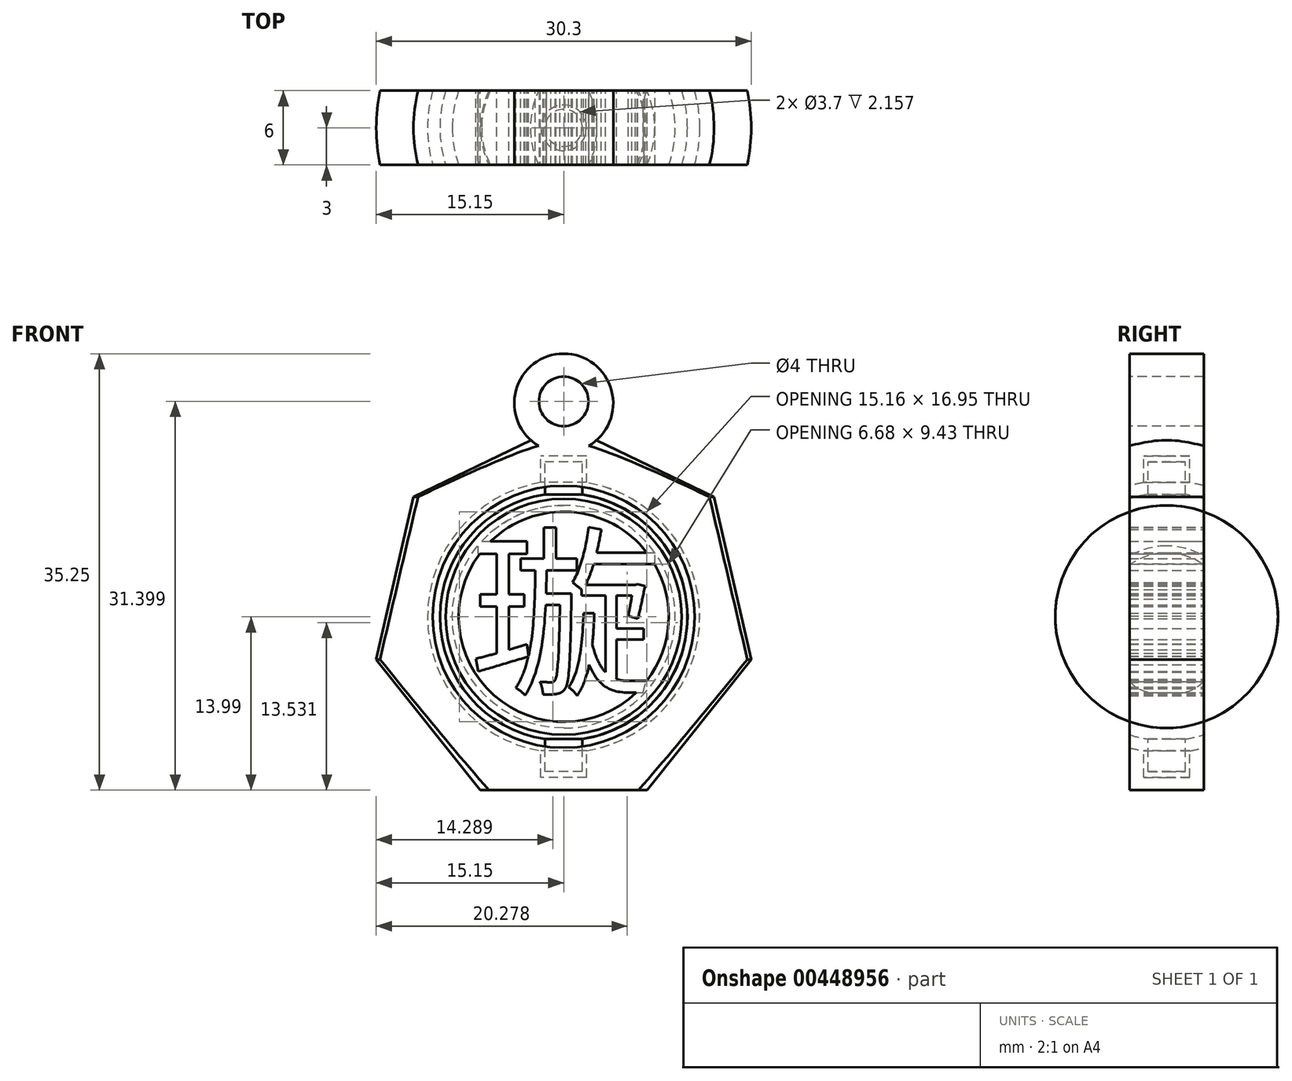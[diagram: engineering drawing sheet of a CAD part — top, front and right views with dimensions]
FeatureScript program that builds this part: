
annotation { "Feature Type Name" : "Feature", "Feature Type Description" : "" }
export const myFeature = defineFeature(function(context is Context, id is Id, definition is map)
    precondition{}
    {
        {
            var Q0;
            Q0=qCreatedBy(makeId("Front.planeOp"),FACE);
            var sketch = newSketch(context, id + "F0", { "sketchPlane" : qUnion([Q0])});
            skLineSegment(sketch, "E0.bottom", {"start": v(1.85, -13) * mm, "end": v(-1.85, -13) * mm});
            skLineSegment(sketch, "E0.top", {"start": v(1.85, 13) * mm, "end": v(-1.85, 13) * mm});
            skLineSegment(sketch, "E0.left", {"start": v(1.85, -13) * mm, "end": v(1.85, 13) * mm});
            skLineSegment(sketch, "E0.right", {"start": v(-1.85, -13) * mm, "end": v(-1.85, 13) * mm});
            skPoint(sketch, "E0.middle", {"position": v(0, 0) * mm});
            skLineSegment(sketch, "E1.bottom", {"start": v(1.5, -12.5) * mm, "end": v(-1.5, -12.5) * mm});
            skLineSegment(sketch, "E1.top", {"start": v(1.5, 12.5) * mm, "end": v(-1.5, 12.5) * mm});
            skLineSegment(sketch, "E1.left", {"start": v(1.5, -12.5) * mm, "end": v(1.5, 12.5) * mm});
            skLineSegment(sketch, "E1.right", {"start": v(-1.5, -12.5) * mm, "end": v(-1.5, 12.5) * mm});
            skCircle(sketch, "E2", {"center": v(0, 0) * mm, "radius": 10 * mm});
            skCircle(sketch, "E3", {"center": v(0, 0) * mm, "radius": 11 * mm});
            skCircle(sketch, "E4.cCircle", {"center": v(0, 0) * mm, "radius": 14 * mm});
            skLineSegment(sketch, "E4.0", {"start": v(15.15, -3.46) * mm, "end": v(6.74, -14) * mm});
            skLineSegment(sketch, "E4.1", {"start": v(6.74, -14) * mm, "end": v(-6.74, -14) * mm});
            skLineSegment(sketch, "E4.2", {"start": v(-6.74, -14) * mm, "end": v(-15.15, -3.46) * mm});
            skLineSegment(sketch, "E4.3", {"start": v(-15.15, -3.46) * mm, "end": v(-12.15, 9.69) * mm});
            skLineSegment(sketch, "E4.4", {"start": v(-12.15, 9.69) * mm, "end": v(0, 15.54) * mm});
            skLineSegment(sketch, "E4.5", {"start": v(0, 15.54) * mm, "end": v(12.15, 9.69) * mm});
            skLineSegment(sketch, "E4.6", {"start": v(12.15, 9.69) * mm, "end": v(15.15, -3.46) * mm});
            skPoint(sketch, "E4.0.midPoint", {"position": v(10.95, -8.73) * mm});
            skCircle(sketch, "E5", {"center": v(0, 0) * mm, "radius": 9 * mm});
            skSolve(sketch);
        }
        {
            var Q0;
            Q0=qCreatedBy(makeId("Front.planeOp"),FACE);
            var sketch = newSketch(context, id + "F1", { "sketchPlane" : qUnion([Q0])});
            skLineSegment(sketch, "E6.0", {"start": v(1.85, -13) * mm, "end": v(-1.85, -13) * mm});
            skLineSegment(sketch, "E6.1", {"start": v(1.85, 13) * mm, "end": v(-1.85, 13) * mm});
            skLineSegment(sketch, "E6.2", {"start": v(1.85, -13) * mm, "end": v(1.85, -10.84) * mm});
            skLineSegment(sketch, "E6.3", {"start": v(-1.85, -13) * mm, "end": v(-1.85, -10.84) * mm});
            skPoint(sketch, "E6.4", {"position": v(0, 0) * mm});
            skLineSegment(sketch, "E6.5", {"start": v(1.5, -12.5) * mm, "end": v(-1.5, -12.5) * mm});
            skLineSegment(sketch, "E6.6", {"start": v(1.5, 12.5) * mm, "end": v(-1.5, 12.5) * mm});
            skLineSegment(sketch, "E6.7", {"start": v(1.5, -12.5) * mm, "end": v(1.5, -9.89) * mm});
            skLineSegment(sketch, "E6.8", {"start": v(-1.5, -12.5) * mm, "end": v(-1.5, -9.89) * mm});
            skPoint(sketch, "E6.9", {"position": v(0, 0) * mm});
            skArc(sketch, "E6.10", {"start": v(-1.5, 9.89) * mm, "mid": v(-10, 0) * mm, "end": v(-1.5, -9.89) * mm});
            skArc(sketch, "E6.11", {"start": v(-1.85, 10.84) * mm, "mid": v(-11, 0) * mm, "end": v(-1.85, -10.84) * mm});
            skLineSegment(sketch, "E6.13", {"start": v(15.15, -3.46) * mm, "end": v(6.74, -14) * mm});
            skLineSegment(sketch, "E6.14", {"start": v(6.74, -14) * mm, "end": v(-6.74, -14) * mm});
            skLineSegment(sketch, "E6.15", {"start": v(-6.74, -14) * mm, "end": v(-15.15, -3.46) * mm});
            skLineSegment(sketch, "E6.16", {"start": v(-15.15, -3.46) * mm, "end": v(-12.15, 9.69) * mm});
            skLineSegment(sketch, "E6.17", {"start": v(-12.15, 9.69) * mm, "end": v(0, 15.54) * mm});
            skLineSegment(sketch, "E6.18", {"start": v(0, 15.54) * mm, "end": v(12.15, 9.69) * mm});
            skLineSegment(sketch, "E6.19", {"start": v(12.15, 9.69) * mm, "end": v(15.15, -3.46) * mm});
            skPoint(sketch, "E6.20", {"position": v(10.95, -8.73) * mm});
            skCircle(sketch, "E6.21", {"center": v(0, 0) * mm, "radius": 9 * mm});
            skLineSegment(sketch, "E7.trimOffspring", {"start": v(-1.85, 10.84) * mm, "end": v(-1.85, 13) * mm});
            skLineSegment(sketch, "E8.trimOffspring", {"start": v(-1.5, 9.89) * mm, "end": v(-1.5, 12.5) * mm});
            skLineSegment(sketch, "E9.trimOffspring", {"start": v(1.85, 10.84) * mm, "end": v(1.85, 13) * mm});
            skLineSegment(sketch, "E10.trimOffspring", {"start": v(1.5, 9.89) * mm, "end": v(1.5, 12.5) * mm});
            skArc(sketch, "E11.trimOffspring", {"start": v(1.85, -10.84) * mm, "mid": v(11, 0) * mm, "end": v(1.85, 10.84) * mm});
            skArc(sketch, "E12.trimOffspring", {"start": v(1.5, -9.89) * mm, "mid": v(10, 0) * mm, "end": v(1.5, 9.89) * mm});
            skSolve(sketch);
        }
        {
            var Q0;
            Q0=qCreatedBy(makeId("Front.planeOp"),FACE);
            var sketch = newSketch(context, id + "F2", { "sketchPlane" : qUnion([Q0])});
            skLineSegment(sketch, "E13.0", {"start": v(1.85, -13) * mm, "end": v(-1.85, -13) * mm});
            skLineSegment(sketch, "E13.1", {"start": v(1.85, 13) * mm, "end": v(-1.85, 13) * mm});
            skLineSegment(sketch, "E13.2", {"start": v(1.85, -13) * mm, "end": v(1.85, -10.84) * mm});
            skLineSegment(sketch, "E13.3", {"start": v(-1.85, -13) * mm, "end": v(-1.85, -10.84) * mm});
            skPoint(sketch, "E13.4", {"position": v(0, 0) * mm});
            skLineSegment(sketch, "E13.5", {"start": v(1.5, -12.5) * mm, "end": v(-1.5, -12.5) * mm});
            skLineSegment(sketch, "E13.6", {"start": v(1.5, 12.5) * mm, "end": v(-1.5, 12.5) * mm});
            skLineSegment(sketch, "E13.7", {"start": v(1.5, -12.5) * mm, "end": v(1.5, -9.89) * mm});
            skLineSegment(sketch, "E13.8", {"start": v(-1.5, -12.5) * mm, "end": v(-1.5, -9.89) * mm});
            skPoint(sketch, "E13.9", {"position": v(0, 0) * mm});
            skArc(sketch, "E13.10", {"start": v(-1.5, 9.89) * mm, "mid": v(-10, 0) * mm, "end": v(-1.5, -9.89) * mm});
            skArc(sketch, "E13.11", {"start": v(-1.85, 10.84) * mm, "mid": v(-11, 0) * mm, "end": v(-1.85, -10.84) * mm});
            skLineSegment(sketch, "E13.12", {"start": v(15.15, -3.46) * mm, "end": v(6.74, -14) * mm});
            skLineSegment(sketch, "E13.13", {"start": v(6.74, -14) * mm, "end": v(-6.74, -14) * mm});
            skLineSegment(sketch, "E13.14", {"start": v(-6.74, -14) * mm, "end": v(-15.15, -3.46) * mm});
            skLineSegment(sketch, "E13.15", {"start": v(-15.15, -3.46) * mm, "end": v(-12.15, 9.69) * mm});
            skLineSegment(sketch, "E13.16", {"start": v(-12.15, 9.69) * mm, "end": v(0, 15.54) * mm});
            skLineSegment(sketch, "E13.17", {"start": v(0, 15.54) * mm, "end": v(12.15, 9.69) * mm});
            skLineSegment(sketch, "E13.18", {"start": v(12.15, 9.69) * mm, "end": v(15.15, -3.46) * mm});
            skPoint(sketch, "E13.19", {"position": v(10.95, -8.73) * mm});
            skCircle(sketch, "E13.20", {"center": v(0, 0) * mm, "radius": 9 * mm});
            skLineSegment(sketch, "E13.21", {"start": v(-1.85, 10.84) * mm, "end": v(-1.85, 13) * mm});
            skLineSegment(sketch, "E13.22", {"start": v(-1.5, 9.89) * mm, "end": v(-1.5, 12.5) * mm});
            skLineSegment(sketch, "E13.23", {"start": v(1.85, 10.84) * mm, "end": v(1.85, 13) * mm});
            skLineSegment(sketch, "E13.24", {"start": v(1.5, 9.89) * mm, "end": v(1.5, 12.5) * mm});
            skArc(sketch, "E13.25", {"start": v(1.85, -10.84) * mm, "mid": v(11, 0) * mm, "end": v(1.85, 10.84) * mm});
            skArc(sketch, "E13.26", {"start": v(1.5, -9.89) * mm, "mid": v(10, 0) * mm, "end": v(1.5, 9.89) * mm});
            skLineSegment(sketch, "E14", {"start": v(0, 15.54) * mm, "end": v(0, -14) * mm});
            skSolve(sketch);
        }
        {
            var Q0;
            Q0=qCreatedBy(makeId("Front.planeOp"),FACE);
            var sketch = newSketch(context, id + "F3", { "sketchPlane" : qUnion([Q0])});
            skLineSegment(sketch, "E15.0", {"start": v(1.85, -13) * mm, "end": v(0, -13) * mm});
            skLineSegment(sketch, "E15.1", {"start": v(1.85, 13) * mm, "end": v(0, 13) * mm});
            skLineSegment(sketch, "E15.2", {"start": v(1.85, -13) * mm, "end": v(1.85, -10.84) * mm});
            skPoint(sketch, "E15.4", {"position": v(0, 0) * mm});
            skLineSegment(sketch, "E15.5", {"start": v(1.5, -12.5) * mm, "end": v(0, -12.5) * mm});
            skLineSegment(sketch, "E15.6", {"start": v(1.5, 12.5) * mm, "end": v(0, 12.5) * mm});
            skLineSegment(sketch, "E15.7", {"start": v(1.5, -12.5) * mm, "end": v(1.5, -9.89) * mm});
            skPoint(sketch, "E15.9", {"position": v(0, 0) * mm});
            skLineSegment(sketch, "E15.12", {"start": v(15.15, -3.46) * mm, "end": v(6.74, -14) * mm});
            skLineSegment(sketch, "E15.13", {"start": v(6.74, -14) * mm, "end": v(0, -14) * mm});
            skLineSegment(sketch, "E15.17", {"start": v(0, 15.54) * mm, "end": v(12.15, 9.69) * mm});
            skLineSegment(sketch, "E15.18", {"start": v(12.15, 9.69) * mm, "end": v(15.15, -3.46) * mm});
            skPoint(sketch, "E15.19", {"position": v(10.95, -8.73) * mm});
            skArc(sketch, "E15.20", {"start": v(0, -9) * mm, "mid": v(9, 0) * mm, "end": v(0, 9) * mm});
            skLineSegment(sketch, "E15.23", {"start": v(1.85, 10.84) * mm, "end": v(1.85, 13) * mm});
            skLineSegment(sketch, "E15.24", {"start": v(1.5, 9.89) * mm, "end": v(1.5, 12.5) * mm});
            skArc(sketch, "E15.25", {"start": v(1.85, -10.84) * mm, "mid": v(11, 0) * mm, "end": v(1.85, 10.84) * mm});
            skArc(sketch, "E15.26", {"start": v(1.5, -9.89) * mm, "mid": v(10, 0) * mm, "end": v(1.5, 9.89) * mm});
            skLineSegment(sketch, "E15.27", {"start": v(0, 15.54) * mm, "end": v(0, 13) * mm});
            skPoint(sketch, "E15.16.end.orphan", {"position": v(0, 15.54) * mm});
            skPoint(sketch, "E15.16.start.orphan", {"position": v(-12.15, 9.69) * mm});
            skPoint(sketch, "E15.15.end.orphan", {"position": v(-12.15, 9.69) * mm});
            skPoint(sketch, "E15.15.start.orphan", {"position": v(-15.15, -3.46) * mm});
            skPoint(sketch, "E15.14.end.orphan", {"position": v(-15.15, -3.46) * mm});
            skPoint(sketch, "E15.14.start.orphan", {"position": v(-6.74, -14) * mm});
            skPoint(sketch, "E15.11.end.orphan", {"position": v(-1.85, -10.84) * mm});
            skPoint(sketch, "E15.11.start.orphan", {"position": v(-1.85, 10.84) * mm});
            skPoint(sketch, "E15.10.end.orphan", {"position": v(-1.5, -9.89) * mm});
            skPoint(sketch, "E15.10.start.orphan", {"position": v(-1.5, 9.89) * mm});
            skPoint(sketch, "E15.22.end.orphan", {"position": v(-1.5, 12.5) * mm});
            skPoint(sketch, "E15.22.start.orphan", {"position": v(-1.5, 9.89) * mm});
            skPoint(sketch, "E15.21.end.orphan", {"position": v(-1.85, 13) * mm});
            skPoint(sketch, "E15.21.start.orphan", {"position": v(-1.85, 10.84) * mm});
            skPoint(sketch, "E15.3.end.orphan", {"position": v(-1.85, -10.84) * mm});
            skPoint(sketch, "E15.3.start.orphan", {"position": v(-1.85, -13) * mm});
            skPoint(sketch, "E15.8.end.orphan", {"position": v(-1.5, -9.89) * mm});
            skPoint(sketch, "E15.8.start.orphan", {"position": v(-1.5, -12.5) * mm});
            skLineSegment(sketch, "E16.trimOffspring", {"start": v(0, -13) * mm, "end": v(0, -14) * mm});
            skLineSegment(sketch, "E17.trimOffspring", {"start": v(0, 12.5) * mm, "end": v(0, 9) * mm});
            skLineSegment(sketch, "E18.trimOffspring", {"start": v(0, -9) * mm, "end": v(0, -12.5) * mm});
            skSolve(sketch);
        }
        {
            var Q0;
            Q0=qSketchRegion(id+"F3",true);
            var Q1;
            Q1=sQuery(id+"F3.wireOp",EDGE,"E17.trimOffspring");
            revolve(context, id + "F4", {"entities" : qUnion([Q0]), "axis" : qUnion([Q1]), "revolveType" : RevolveType.FULL});
        }
        {
            var Q0;
            Q0=qCreatedBy(makeId("Right.planeOp"),FACE);
            var sketch = newSketch(context, id + "F5", { "sketchPlane" : qUnion([Q0])});
            skLineSegment(sketch, "E19.bottom", {"start": v(-25.28, 28.1) * mm, "end": v(-3, 28.1) * mm});
            skLineSegment(sketch, "E19.top", {"start": v(-25.28, -25.85) * mm, "end": v(-3, -25.85) * mm});
            skLineSegment(sketch, "E19.left", {"start": v(-25.28, 28.1) * mm, "end": v(-25.28, -25.85) * mm});
            skLineSegment(sketch, "E19.right", {"start": v(-3, 28.1) * mm, "end": v(-3, -25.85) * mm});
            skLineSegment(sketch, "E20.MirrorCS", {"start": v(25.28, 28.1) * mm, "end": v(25.28, -25.85) * mm});
            skLineSegment(sketch, "E21.MirrorCS", {"start": v(3, 28.1) * mm, "end": v(3, -25.85) * mm});
            skLineSegment(sketch, "E22.MirrorCS", {"start": v(25.28, 28.1) * mm, "end": v(3, 28.1) * mm});
            skLineSegment(sketch, "E23.MirrorCS", {"start": v(25.28, -25.85) * mm, "end": v(3, -25.85) * mm});
            skSolve(sketch);
        }
        {
            var Q0;
            Q0=qSketchRegion(id+"F5",true);
            extrude(context, id + "F6", {"entities" : qUnion([Q0]), "operationType" : NewBodyOperationType.REMOVE, "endBound" : BoundingType.SYMMETRIC, "oppositeDirection" : true, "depth" : 60 * mm});
        }
        {
            var Q0;
            Q0=qCreatedBy(makeId("Front.planeOp"),FACE);
            var sketch = newSketch(context, id + "F7", { "sketchPlane" : qUnion([Q0])});
            skCircle(sketch, "E24", {"center": v(0, 17.25) * mm, "radius": 4 * mm});
            skSolve(sketch);
        }
        {
            var Q0;
            Q0=qSketchRegion(id+"F7",true);
            extrude(context, id + "F8", {"entities" : qUnion([Q0]), "operationType" : NewBodyOperationType.ADD, "endBound" : BoundingType.SYMMETRIC, "depth" : 6 * mm});
        }
        {
            var Q0;
            Q0=qCreatedBy(makeId("Front.planeOp"),FACE);
            var sketch = newSketch(context, id + "F9", { "sketchPlane" : qUnion([Q0])});
            skCircle(sketch, "E25", {"center": v(0, 17.4) * mm, "radius": 2 * mm});
            skSolve(sketch);
        }
        {
            var Q0;
            Q0=qSketchRegion(id+"F9",true);
            extrude(context, id + "F10", {"entities" : qUnion([Q0]), "operationType" : NewBodyOperationType.REMOVE, "endBound" : BoundingType.SYMMETRIC, "oppositeDirection" : true, "depth" : 25 * mm});
        }
        {
            var Q0;
            Q0=qCreatedBy(makeId("Front.planeOp"),FACE);
            var sketch = newSketch(context, id + "F11", { "sketchPlane" : qUnion([Q0])});
            skText(sketch, "E26", { "text": "璇", "fontName": "NotoSansCJKjp-Regular.otf"});
            const initialGuessF11  = {"E26": [-0.00763, -0.00523, 1, 0, 0.01073]};
            skSetInitialGuess(sketch, initialGuessF11);
            skSolve(sketch);
        }
        {
            var Q0;
            Q0 = qSketchRegion(id + "F11", true);
            extrude(context, id + "F12", {"entities" : qUnion([Q0]), "operationType" : NewBodyOperationType.ADD, "endBound" : BoundingType.SYMMETRIC, "depth" : 6 * mm});
        }
        {
            var Q0;
            Q0=qCreatedBy(makeId("Front.planeOp"),FACE);
            var sketch = newSketch(context, id + "F13", { "sketchPlane" : qUnion([Q0])});
            skLineSegment(sketch, "E27.bottom", {"start": v(6.53, 4.24) * mm, "end": v(7.38, 4.24) * mm});
            skLineSegment(sketch, "E27.top", {"start": v(6.53, 5.18) * mm, "end": v(7.38, 5.18) * mm});
            skLineSegment(sketch, "E27.left", {"start": v(6.53, 4.24) * mm, "end": v(6.53, 5.18) * mm});
            skLineSegment(sketch, "E27.right", {"start": v(7.38, 4.24) * mm, "end": v(7.38, 5.18) * mm});
            skSolve(sketch);
        }
        {
            var Q0;
            Q0 = qSketchRegion(id + "F13", true);
            extrude(context, id + "F14", {"entities" : qUnion([Q0]), "operationType" : NewBodyOperationType.ADD, "endBound" : BoundingType.SYMMETRIC, "depth" : 6 * mm});
        }
    });
